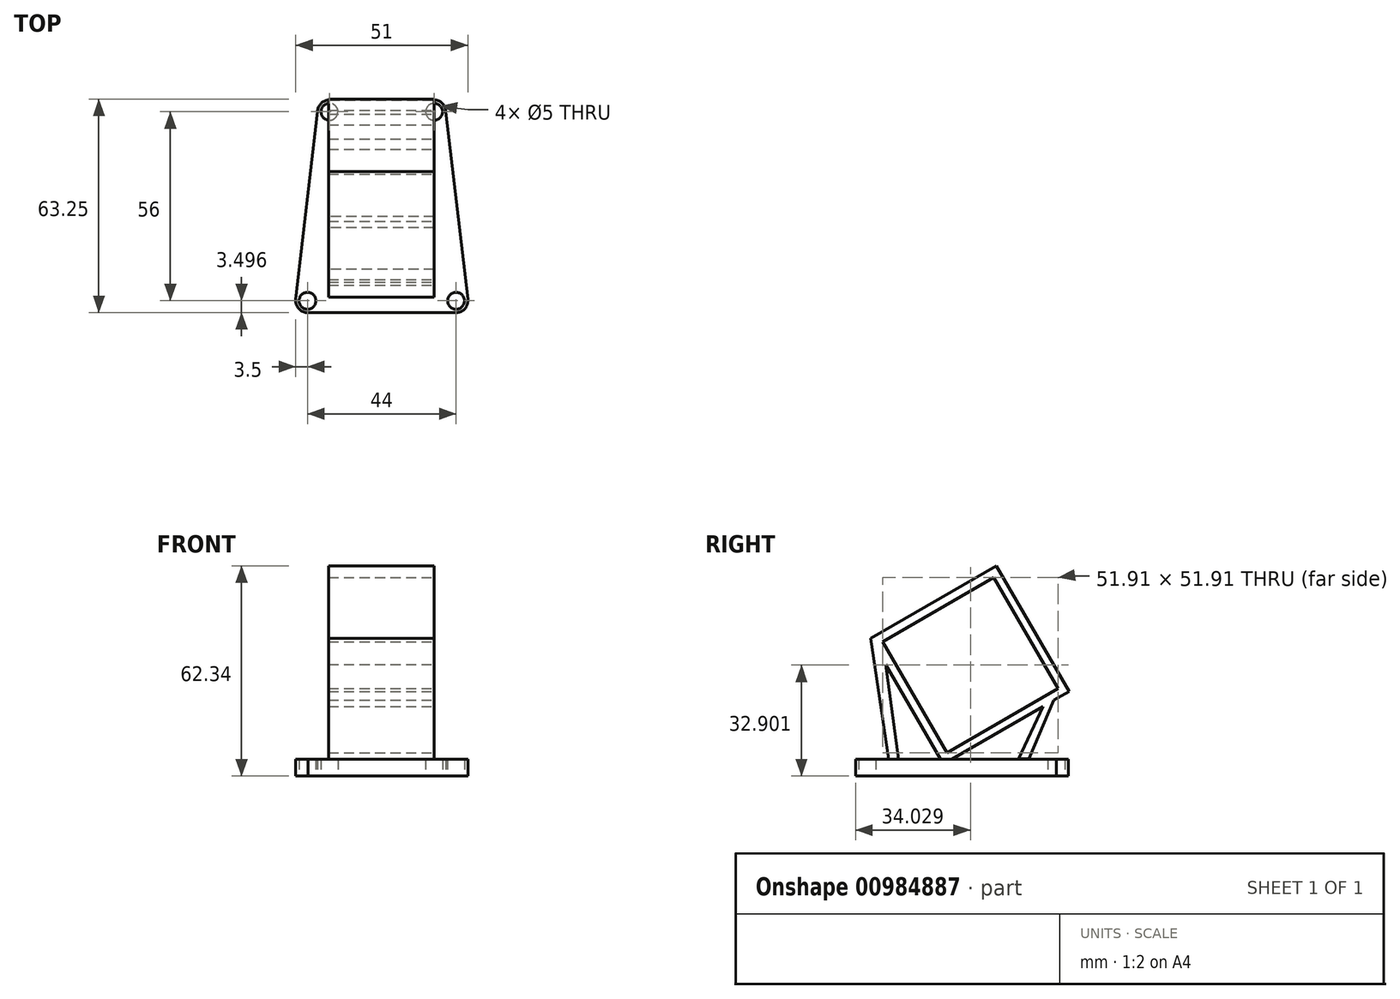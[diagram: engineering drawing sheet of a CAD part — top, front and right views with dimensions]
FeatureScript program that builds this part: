
annotation { "Feature Type Name" : "Feature", "Feature Type Description" : "" }
export const myFeature = defineFeature(function(context is Context, id is Id, definition is map)
    precondition{}
    {
        {
            var Q0;
            Q0=qCreatedBy(makeId("Top.planeOp"),FACE);
            var sketch = newSketch(context, id + "F0", { "sketchPlane" : qUnion([Q0])});
            skLineSegment(sketch, "E0", {"start": v(0, 28.6) * mm, "end": v(0, -49.52) * mm, "construction": true});
            skLineSegment(sketch, "E1", {"start": v(0, 17.7) * mm, "end": v(15.5, 17.7) * mm, "construction": true});
            skLineSegment(sketch, "E2", {"start": v(0, 17.7) * mm, "end": v(-15.5, 17.7) * mm, "construction": true});
            skLineSegment(sketch, "E3", {"start": v(-15.5, 17.7) * mm, "end": v(-15.5, -38.3) * mm, "construction": true});
            skLineSegment(sketch, "E4", {"start": v(15.5, 17.7) * mm, "end": v(15.5, -38.3) * mm, "construction": true});
            skLineSegment(sketch, "E5", {"start": v(0, -38.3) * mm, "end": v(-30.58, -38.3) * mm, "construction": true});
            skLineSegment(sketch, "E6", {"start": v(0, -38.3) * mm, "end": v(28.83, -38.3) * mm, "construction": true});
            skLineSegment(sketch, "E7", {"start": v(-15.5, 17.7) * mm, "end": v(-15.5, 23.7) * mm, "construction": true});
            skLineSegment(sketch, "E8", {"start": v(-15.5, -35.05) * mm, "end": v(-22, -35.05) * mm, "construction": true});
            skLineSegment(sketch, "E9", {"start": v(15.5, -35.95) * mm, "end": v(22, -35.95) * mm, "construction": true});
            skLineSegment(sketch, "E10", {"start": v(-22, -35.05) * mm, "end": v(-22, -40.14) * mm, "construction": true});
            skLineSegment(sketch, "E11", {"start": v(22, -35.95) * mm, "end": v(22, -39.66) * mm, "construction": true});
            skLineSegment(sketch, "E12", {"start": v(-15.5, 17.7) * mm, "end": v(-30.62, 17.7) * mm, "construction": true});
            skLineSegment(sketch, "E13", {"start": v(15.5, 17.7) * mm, "end": v(31.9, 17.7) * mm, "construction": true});
            skPoint(sketch, "E14", {"position": v(-15.5, 17.7) * mm});
            skPoint(sketch, "E15", {"position": v(0, 17.7) * mm});
            skPoint(sketch, "E16", {"position": v(15.5, 17.7) * mm});
            skPoint(sketch, "E17", {"position": v(-15.5, -38.3) * mm});
            skPoint(sketch, "E18", {"position": v(15.5, -38.3) * mm});
            skPoint(sketch, "E19", {"position": v(-22, -38.3) * mm});
            skPoint(sketch, "E20", {"position": v(22, -38.3) * mm});
            skSolve(sketch);
        }
        {
            var Q0;
            Q0=qCreatedBy(makeId("Top.planeOp"),FACE);
            var sketch = newSketch(context, id + "F1", { "sketchPlane" : qUnion([Q0])});
            skCircle(sketch, "E21", {"center": v(-15.5, 17.73) * mm, "radius": 3.5 * mm});
            skCircle(sketch, "E22", {"center": v(15.49, 17.73) * mm, "radius": 3.5 * mm});
            skCircle(sketch, "E23", {"center": v(-22, -38.3) * mm, "radius": 3.5 * mm});
            skCircle(sketch, "E24", {"center": v(22, -38.29) * mm, "radius": 3.5 * mm});
            skLineSegment(sketch, "E25", {"start": v(-15.49, 21.23) * mm, "end": v(15.49, 21.23) * mm});
            skLineSegment(sketch, "E26", {"start": v(18.99, 17.73) * mm, "end": v(25.47, -37.88) * mm});
            skLineSegment(sketch, "E27", {"start": v(-19, 17.73) * mm, "end": v(-25.48, -37.89) * mm});
            skLineSegment(sketch, "E28", {"start": v(-22.16, -41.8) * mm, "end": v(22, -41.79) * mm});
            skSolve(sketch);
        }
        {
            var Q0;
            Q0=qSketchRegion(id+"F1",true);
            extrude(context, id + "F2", {"entities" : qUnion([Q0]), "depth" : 5 * mm, "offsetDistance" : 25 * mm});
        }
        {
            var Q0;
            Q0=sQuery(id+"F0.wireOp",VERTEX,"E14");
            var Q1;
            Q1=sQuery(id+"F0.wireOp",VERTEX,"E16");
            var Q2;
            Q2=sQuery(id+"F0.wireOp",VERTEX,"E19");
            var Q3;
            Q3=sQuery(id+"F0.wireOp",VERTEX,"E20");
            var Q4;
            Q4=makeQuery(id+"F2.opExtrude","SWEPT_BODY",BODY,{"disambiguationData":[OSD([sQuery(id+"F1.wireOp",EDGE,"E21"),sQuery(id+"F1.wireOp",EDGE,"E22"),sQuery(id+"F1.wireOp",EDGE,"E23"),sQuery(id+"F1.wireOp",EDGE,"E24"),sQuery(id+"F1.wireOp",EDGE,"E25"),sQuery(id+"F1.wireOp",EDGE,"E26"),sQuery(id+"F1.wireOp",EDGE,"E27"),sQuery(id+"F1.wireOp",EDGE,"E28")])]});
            hole(context, id + "F3", {"style" : HoleStyle.SIMPLE, "endStyle" : HoleEndStyle.THROUGH, "oppositeDirection" : true, "holeDiameter" : 5 * mm, "majorDiameter" : 5 * mm, "isTappedThrough" : true, "tappedDepth" : 12 * mm, "tapClearance" : 3, "startFromSketch" : true, "locations" : qUnion([Q0, Q1, Q2, Q3]), "scope" : qUnion([Q4])});
        }
        {
            var Q0;
            Q0=qCreatedBy(makeId("Right.planeOp"),FACE);
            cPlane(context, id + "F4", {"entities" : qUnion([Q0]), "cplaneType" : CPlaneType.OFFSET, "offset" : 15.5 * mm, "width" : 150 * mm, "height" : 150 * mm});
        }
        {
            var Q0;
            Q0=qCreatedBy(id+"F4.planeOp",FACE);
            var sketch = newSketch(context, id + "F5", { "sketchPlane" : qUnion([Q0])});
            skLineSegment(sketch, "E29", {"start": v(18.2, 25.95) * mm, "end": v(-14.72, 6.95) * mm, "construction": true});
            skLineSegment(sketch, "E30", {"start": v(-14.72, 6.95) * mm, "end": v(-33.72, 39.86) * mm, "construction": true});
            skLineSegment(sketch, "E31", {"start": v(-14.72, 6.95) * mm, "end": v(-33.72, 39.86) * mm});
            skLineSegment(sketch, "E32", {"start": v(-33.72, 39.86) * mm, "end": v(-0.8, 58.86) * mm});
            skLineSegment(sketch, "E33", {"start": v(-0.8, 58.86) * mm, "end": v(18.2, 25.95) * mm});
            skLineSegment(sketch, "E34", {"start": v(-14.72, 6.95) * mm, "end": v(18.2, 25.95) * mm});
            skLineSegment(sketch, "E35", {"start": v(-15.78, 3.6) * mm, "end": v(-37.28, 40.84) * mm, "construction": true});
            skLineSegment(sketch, "E36", {"start": v(-37.28, 40.84) * mm, "end": v(-0.04, 62.34) * mm});
            skLineSegment(sketch, "E37", {"start": v(-0.04, 62.34) * mm, "end": v(21.46, 25.1) * mm});
            skLineSegment(sketch, "E38", {"start": v(-15.78, 3.6) * mm, "end": v(21.46, 25.1) * mm});
            skLineSegment(sketch, "E39", {"start": v(-15.78, 3.6) * mm, "end": v(-37.28, 40.84) * mm});
            skLineSegment(sketch, "E40", {"start": v(-37.28, 40.84) * mm, "end": v(-31.8, 3.6) * mm});
            skLineSegment(sketch, "E41", {"start": v(-31.8, 3.6) * mm, "end": v(-28.8, 3.6) * mm});
            skLineSegment(sketch, "E42", {"start": v(-28.8, 3.6) * mm, "end": v(-33.72, 39.86) * mm});
            skLineSegment(sketch, "E43", {"start": v(13.8, 20.67) * mm, "end": v(6.58, 5.08) * mm});
            skLineSegment(sketch, "E44", {"start": v(6.58, 5.08) * mm, "end": v(9.58, 5.08) * mm});
            skLineSegment(sketch, "E45", {"start": v(9.58, 5.08) * mm, "end": v(16.99, 22.52) * mm});
            skLineSegment(sketch, "E46", {"start": v(16.99, 22.52) * mm, "end": v(13.8, 20.67) * mm});
            skSolve(sketch);
        }
        {
            var Q0;
            {var subQ0=sQuery(id+"F5.wireOp",EDGE,"E40");Q0=makeQuery(id+"F5.imprint","IMPRINT",FACE,{"disambiguationData":[TD([[makeQuery(id+"F5.imprint","IMPRINT",EDGE,{"derivedFrom":subQ0}),1.0]])]});}
            var Q1;
            Q1=makeQuery(id+"F5.imprint","IMPRINT",FACE,{"disambiguationData":[TD([[makeQuery(id+"F5.imprint","IMPRINT",EDGE,{"derivedFrom":sQuery(id+"F5.wireOp",EDGE,"E31")}),1.0]])]});
            var Q2;
            {var subQ2=sQuery(id+"F5.wireOp",EDGE,"E43");Q2=makeQuery(id+"F5.imprint","IMPRINT",FACE,{"disambiguationData":[TD([[makeQuery(id+"F5.imprint","IMPRINT",EDGE,{"derivedFrom":subQ2}),1.0]])]});}
            extrude(context, id + "F6", {"entities" : qUnion([Q0, Q1, Q2]), "operationType" : NewBodyOperationType.ADD, "oppositeDirection" : true, "depth" : 31.3 * mm, "offsetDistance" : 25 * mm});
        }
    });
